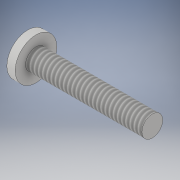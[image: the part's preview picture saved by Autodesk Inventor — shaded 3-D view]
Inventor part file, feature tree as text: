
AUTODESK INVENTOR PART (.ipt)
format: ipt  version: 2019 (Build 230136000, 136)  size: 106,496 bytes
history: native  units: in
note: dims shown in document units (in); Inventor stores cm internally (conversion verified against a paired STEP export)
features: extrude x2, sketch x1, thread x1
ambient origin geometry x8: Origin, YZ Plane, XZ Plane, XY Plane, X Axis, Y Axis, Z Axis, Center Point
bodies: Solid1 (feature_tree)
feature tree (4):
  sketch  "Sketch1"  dims[d0=0.25in d1=0.125in d2=0.75in d3=0.0in d4=0.05in d5=0.0in d6=1.0in d7=0.0in]
  extrude  "Extrusion1"  Depth=0.125in
  extrude  "Extrusion2"  Depth=0.75in TaperAngle=0.0deg
  thread  "Thread1"  [1 undecoded]
note: 1 required parameter value undecoded (feature->parameter linkage not recoverable at this tier; creation-order binding heuristic only, values carry confidence <= 0.55)
